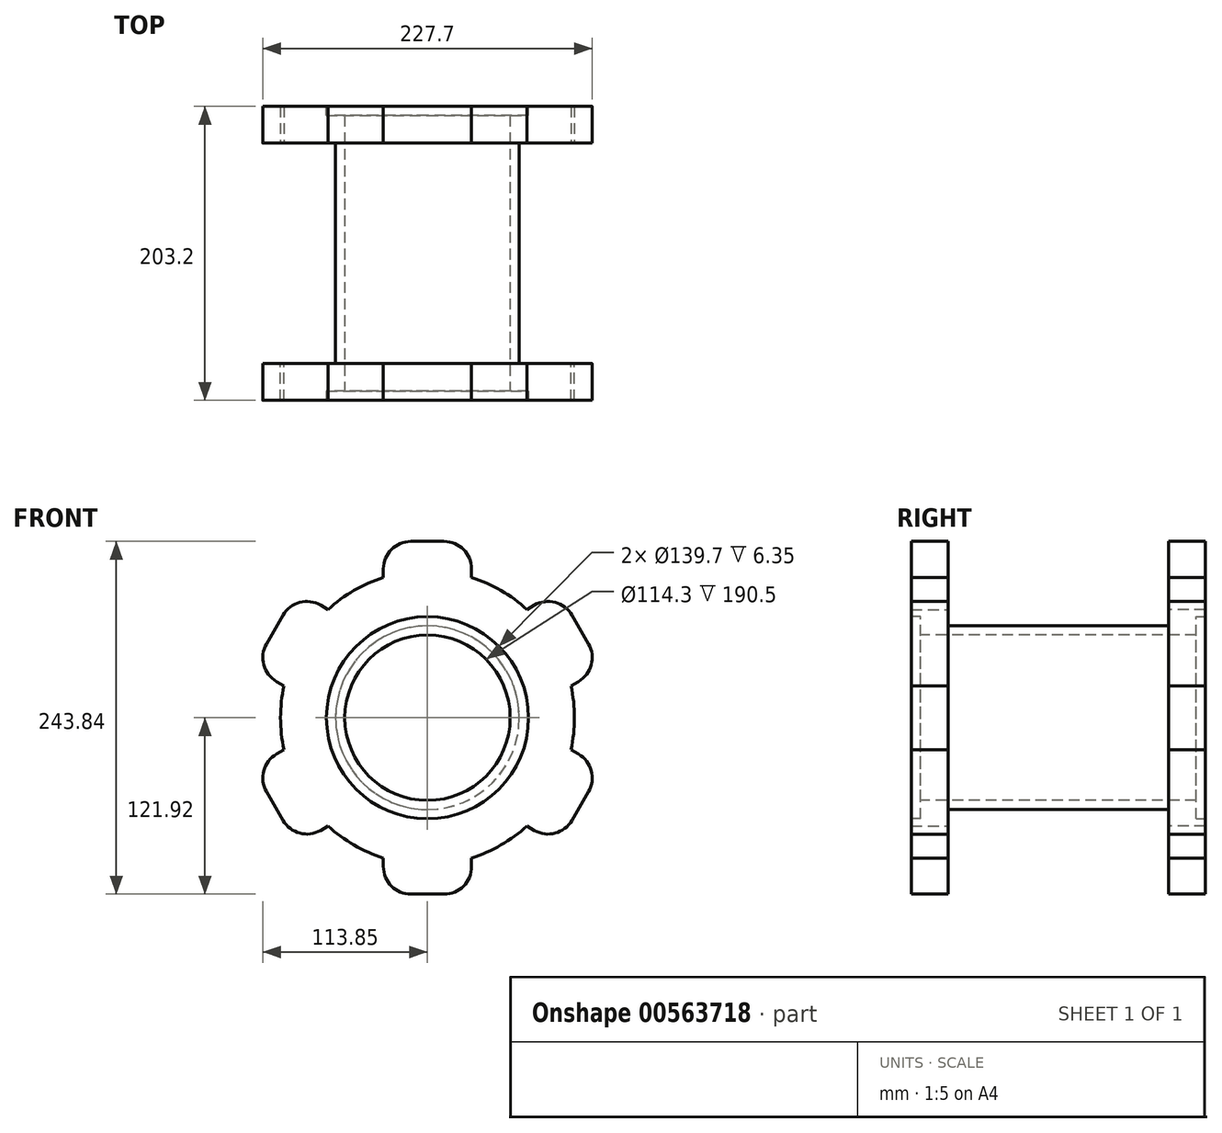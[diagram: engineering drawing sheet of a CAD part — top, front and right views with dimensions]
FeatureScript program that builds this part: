
annotation { "Feature Type Name" : "Feature", "Feature Type Description" : "" }
export const myFeature = defineFeature(function(context is Context, id is Id, definition is map)
    precondition{}
    {
        {
            var Q0;
            Q0=qCreatedBy(makeId("Front.planeOp"),FACE);
            var sketch = newSketch(context, id + "F0", { "sketchPlane" : qUnion([Q0])});
            skCircle(sketch, "E0", {"center": v(0, 0) * mm, "radius": 101.6 * mm});
            skLineSegment(sketch, "E1.top", {"start": v(11.43, 121.92) * mm, "end": v(-11.43, 121.92) * mm});
            skLineSegment(sketch, "E1.left", {"start": v(30.48, 96.92) * mm, "end": v(30.48, 102.87) * mm});
            skLineSegment(sketch, "E1.right", {"start": v(-30.48, 96.92) * mm, "end": v(-30.48, 102.87) * mm});
            skPoint(sketch, "E2.visualSharp", {"position": v(30.48, 121.92) * mm});
            skArc(sketch, "E2.filletArc", {"start": v(30.48, 102.87) * mm, "mid": v(24.9, 116.34) * mm, "end": v(11.43, 121.92) * mm});
            skPoint(sketch, "E3.visualSharp", {"position": v(-30.48, 121.92) * mm});
            skArc(sketch, "E3.filletArc", {"start": v(-11.43, 121.92) * mm, "mid": v(-24.9, 116.34) * mm, "end": v(-30.48, 102.87) * mm});
            skLineSegment(sketch, "E4.1.1", {"start": v(-99.18, 22.06) * mm, "end": v(-104.33, 25.04) * mm});
            skPoint(sketch, "E4.1.2", {"position": v(-90.35, 87.36) * mm});
            skLineSegment(sketch, "E4.1.3", {"start": v(-99.87, 70.86) * mm, "end": v(-111.3, 51.06) * mm});
            skPoint(sketch, "E4.1.4", {"position": v(-120.83, 34.56) * mm});
            skArc(sketch, "E4.1.5", {"start": v(-111.3, 51.06) * mm, "mid": v(-113.2, 36.6) * mm, "end": v(-104.33, 25.04) * mm});
            skLineSegment(sketch, "E4.1.6", {"start": v(-68.7, 74.86) * mm, "end": v(-73.85, 77.83) * mm});
            skArc(sketch, "E4.1.7", {"start": v(-73.85, 77.83) * mm, "mid": v(-88.3, 79.73) * mm, "end": v(-99.87, 70.86) * mm});
            skLineSegment(sketch, "E4.2.1", {"start": v(-68.7, -74.86) * mm, "end": v(-73.85, -77.83) * mm});
            skPoint(sketch, "E4.2.2", {"position": v(-120.83, -34.56) * mm});
            skLineSegment(sketch, "E4.2.3", {"start": v(-111.3, -51.06) * mm, "end": v(-99.87, -70.86) * mm});
            skPoint(sketch, "E4.2.4", {"position": v(-90.35, -87.36) * mm});
            skArc(sketch, "E4.2.5", {"start": v(-99.87, -70.86) * mm, "mid": v(-88.3, -79.73) * mm, "end": v(-73.85, -77.83) * mm});
            skLineSegment(sketch, "E4.2.6", {"start": v(-99.18, -22.06) * mm, "end": v(-104.33, -25.04) * mm});
            skArc(sketch, "E4.2.7", {"start": v(-104.33, -25.04) * mm, "mid": v(-113.2, -36.6) * mm, "end": v(-111.3, -51.06) * mm});
            skLineSegment(sketch, "E4.3.1", {"start": v(30.48, -96.92) * mm, "end": v(30.48, -102.87) * mm});
            skPoint(sketch, "E4.3.2", {"position": v(-30.48, -121.92) * mm});
            skLineSegment(sketch, "E4.3.3", {"start": v(-11.43, -121.92) * mm, "end": v(11.43, -121.92) * mm});
            skPoint(sketch, "E4.3.4", {"position": v(30.48, -121.92) * mm});
            skArc(sketch, "E4.3.5", {"start": v(11.43, -121.92) * mm, "mid": v(24.9, -116.34) * mm, "end": v(30.48, -102.87) * mm});
            skLineSegment(sketch, "E4.3.6", {"start": v(-30.48, -96.92) * mm, "end": v(-30.48, -102.87) * mm});
            skArc(sketch, "E4.3.7", {"start": v(-30.48, -102.87) * mm, "mid": v(-24.9, -116.34) * mm, "end": v(-11.43, -121.92) * mm});
            skLineSegment(sketch, "E4.4.1", {"start": v(99.18, -22.06) * mm, "end": v(104.33, -25.04) * mm});
            skPoint(sketch, "E4.4.2", {"position": v(90.35, -87.36) * mm});
            skLineSegment(sketch, "E4.4.3", {"start": v(99.87, -70.86) * mm, "end": v(111.3, -51.06) * mm});
            skPoint(sketch, "E4.4.4", {"position": v(120.83, -34.56) * mm});
            skArc(sketch, "E4.4.5", {"start": v(111.3, -51.06) * mm, "mid": v(113.2, -36.6) * mm, "end": v(104.33, -25.04) * mm});
            skLineSegment(sketch, "E4.4.6", {"start": v(68.7, -74.86) * mm, "end": v(73.85, -77.83) * mm});
            skArc(sketch, "E4.4.7", {"start": v(73.85, -77.83) * mm, "mid": v(88.3, -79.73) * mm, "end": v(99.87, -70.86) * mm});
            skLineSegment(sketch, "E4.5.1", {"start": v(68.7, 74.86) * mm, "end": v(73.85, 77.83) * mm});
            skPoint(sketch, "E4.5.2", {"position": v(120.83, 34.56) * mm});
            skLineSegment(sketch, "E4.5.3", {"start": v(111.3, 51.06) * mm, "end": v(99.87, 70.86) * mm});
            skPoint(sketch, "E4.5.4", {"position": v(90.35, 87.36) * mm});
            skArc(sketch, "E4.5.5", {"start": v(99.87, 70.86) * mm, "mid": v(88.3, 79.73) * mm, "end": v(73.85, 77.83) * mm});
            skLineSegment(sketch, "E4.5.6", {"start": v(99.18, 22.06) * mm, "end": v(104.33, 25.04) * mm});
            skArc(sketch, "E4.5.7", {"start": v(104.33, 25.04) * mm, "mid": v(113.2, 36.6) * mm, "end": v(111.3, 51.06) * mm});
            skSolve(sketch);
        }
        {
            var Q0;
            {var subQ0=sQuery(id+"F0.wireOp",EDGE,"E0");var subQ1=makeQuery(id+"F0.imprint","INTERSECT",VERTEX,{"derivedFrom":[subQ0,sQuery(id+"F0.wireOp",EDGE,"E1.left")]});Q0=makeQuery(id+"F0.imprint","IMPRINT",FACE,{"disambiguationData":[TD([[makeQuery(id+"F0.imprint","IMPRINT",EDGE,{"disambiguationData":[TD([[subQ1,-1.0]])],"derivedFrom":subQ0}),1.0]])]});}
            var Q1;
            Q1=makeQuery(id+"F0.imprint","IMPRINT",FACE,{"disambiguationData":[TD([[makeQuery(id+"F0.imprint","IMPRINT",EDGE,{"derivedFrom":sQuery(id+"F0.wireOp",EDGE,"E1.top")}),1.0]])]});
            var Q2;
            {var subQ0=sQuery(id+"F0.wireOp",EDGE,"E0");var subQ8=makeQuery(id+"F0.imprint","INTERSECT",VERTEX,{"derivedFrom":[sQuery(id+"F0.wireOp",EDGE,"E4.4.1"),subQ0]});Q2=makeQuery(id+"F0.imprint","IMPRINT",FACE,{"disambiguationData":[TD([[makeQuery(id+"F0.imprint","IMPRINT",EDGE,{"disambiguationData":[TD([[subQ8,1.0]])],"derivedFrom":subQ0}),1.0]])]});}
            var Q3;
            {var subQ0=sQuery(id+"F0.wireOp",EDGE,"E4.5.1");Q3=makeQuery(id+"F0.imprint","IMPRINT",FACE,{"disambiguationData":[TD([[makeQuery(id+"F0.imprint","IMPRINT",EDGE,{"derivedFrom":subQ0}),-1.0]])]});}
            var Q4;
            {var subQ1=sQuery(id+"F0.wireOp",EDGE,"E4.4.1");Q4=makeQuery(id+"F0.imprint","IMPRINT",FACE,{"disambiguationData":[TD([[makeQuery(id+"F0.imprint","IMPRINT",EDGE,{"derivedFrom":subQ1}),-1.0]])]});}
            var Q5;
            {var subQ1=sQuery(id+"F0.wireOp",EDGE,"E4.3.1");Q5=makeQuery(id+"F0.imprint","IMPRINT",FACE,{"disambiguationData":[TD([[makeQuery(id+"F0.imprint","IMPRINT",EDGE,{"derivedFrom":subQ1}),-1.0]])]});}
            var Q6;
            {var subQ1=sQuery(id+"F0.wireOp",EDGE,"E4.2.1");Q6=makeQuery(id+"F0.imprint","IMPRINT",FACE,{"disambiguationData":[TD([[makeQuery(id+"F0.imprint","IMPRINT",EDGE,{"derivedFrom":subQ1}),-1.0]])]});}
            var Q7;
            {var subQ2=sQuery(id+"F0.wireOp",EDGE,"E4.1.1");Q7=makeQuery(id+"F0.imprint","IMPRINT",FACE,{"disambiguationData":[TD([[makeQuery(id+"F0.imprint","IMPRINT",EDGE,{"derivedFrom":subQ2}),-1.0]])]});}
            extrude(context, id + "F1", {"entities" : qUnion([Q0, Q1, Q2, Q3, Q4, Q5, Q6, Q7]), "depth" : 25.4 * mm});
        }
        {
            var Q0;
            Q0=makeQuery(id+"F1.opExtrude","CAP_FACE",FACE,{"disambiguationData":[OSD([sQuery(id+"F0.wireOp",EDGE,"E1.top"),sQuery(id+"F0.wireOp",EDGE,"E1.left"),sQuery(id+"F0.wireOp",EDGE,"E1.right"),sQuery(id+"F0.wireOp",EDGE,"E2.filletArc"),sQuery(id+"F0.wireOp",EDGE,"E3.filletArc"),sQuery(id+"F0.wireOp",EDGE,"E4.1.1"),sQuery(id+"F0.wireOp",EDGE,"E4.1.3"),sQuery(id+"F0.wireOp",EDGE,"E4.1.5"),sQuery(id+"F0.wireOp",EDGE,"E4.1.6"),sQuery(id+"F0.wireOp",EDGE,"E4.1.7"),sQuery(id+"F0.wireOp",EDGE,"E4.2.1"),sQuery(id+"F0.wireOp",EDGE,"E4.2.3"),sQuery(id+"F0.wireOp",EDGE,"E4.2.5"),sQuery(id+"F0.wireOp",EDGE,"E4.2.6"),sQuery(id+"F0.wireOp",EDGE,"E4.2.7"),sQuery(id+"F0.wireOp",EDGE,"E4.3.1"),sQuery(id+"F0.wireOp",EDGE,"E4.3.3"),sQuery(id+"F0.wireOp",EDGE,"E4.3.5"),sQuery(id+"F0.wireOp",EDGE,"E4.3.6"),sQuery(id+"F0.wireOp",EDGE,"E4.3.7"),sQuery(id+"F0.wireOp",EDGE,"E4.4.1"),sQuery(id+"F0.wireOp",EDGE,"E4.4.3"),sQuery(id+"F0.wireOp",EDGE,"E4.4.5"),sQuery(id+"F0.wireOp",EDGE,"E4.4.6"),sQuery(id+"F0.wireOp",EDGE,"E4.4.7"),sQuery(id+"F0.wireOp",EDGE,"E0"),sQuery(id+"F0.wireOp",EDGE,"E4.5.1"),sQuery(id+"F0.wireOp",EDGE,"E4.5.3"),sQuery(id+"F0.wireOp",EDGE,"E4.5.5"),sQuery(id+"F0.wireOp",EDGE,"E4.5.6"),sQuery(id+"F0.wireOp",EDGE,"E4.5.7")])],"isStart":true});
            var sketch = newSketch(context, id + "F2", { "sketchPlane" : qUnion([Q0])});
            skCircle(sketch, "E5", {"center": v(0, 0) * mm, "radius": 63.5 * mm});
            skSolve(sketch);
        }
        {
            var Q0;
            Q0=qSketchRegion(id+"F2",true);
            extrude(context, id + "F3", {"entities" : qUnion([Q0]), "operationType" : NewBodyOperationType.ADD, "depth" : 152.4 * mm});
        }
        {
            var Q0;
            Q0=makeQuery(id+"F1.opExtrude","CAP_FACE",FACE,{"disambiguationData":[OSD([sQuery(id+"F0.wireOp",EDGE,"E1.top"),sQuery(id+"F0.wireOp",EDGE,"E1.left"),sQuery(id+"F0.wireOp",EDGE,"E1.right"),sQuery(id+"F0.wireOp",EDGE,"E2.filletArc"),sQuery(id+"F0.wireOp",EDGE,"E3.filletArc"),sQuery(id+"F0.wireOp",EDGE,"E4.1.1"),sQuery(id+"F0.wireOp",EDGE,"E4.1.3"),sQuery(id+"F0.wireOp",EDGE,"E4.1.5"),sQuery(id+"F0.wireOp",EDGE,"E4.1.6"),sQuery(id+"F0.wireOp",EDGE,"E4.1.7"),sQuery(id+"F0.wireOp",EDGE,"E4.2.1"),sQuery(id+"F0.wireOp",EDGE,"E4.2.3"),sQuery(id+"F0.wireOp",EDGE,"E4.2.5"),sQuery(id+"F0.wireOp",EDGE,"E4.2.6"),sQuery(id+"F0.wireOp",EDGE,"E4.2.7"),sQuery(id+"F0.wireOp",EDGE,"E4.3.1"),sQuery(id+"F0.wireOp",EDGE,"E4.3.3"),sQuery(id+"F0.wireOp",EDGE,"E4.3.5"),sQuery(id+"F0.wireOp",EDGE,"E4.3.6"),sQuery(id+"F0.wireOp",EDGE,"E4.3.7"),sQuery(id+"F0.wireOp",EDGE,"E4.4.1"),sQuery(id+"F0.wireOp",EDGE,"E4.4.3"),sQuery(id+"F0.wireOp",EDGE,"E4.4.5"),sQuery(id+"F0.wireOp",EDGE,"E4.4.6"),sQuery(id+"F0.wireOp",EDGE,"E4.4.7"),sQuery(id+"F0.wireOp",EDGE,"E0"),sQuery(id+"F0.wireOp",EDGE,"E4.5.1"),sQuery(id+"F0.wireOp",EDGE,"E4.5.3"),sQuery(id+"F0.wireOp",EDGE,"E4.5.5"),sQuery(id+"F0.wireOp",EDGE,"E4.5.6"),sQuery(id+"F0.wireOp",EDGE,"E4.5.7")])],"isStart":true});
            cPlane(context, id + "F4", {"entities" : qUnion([Q0]), "cplaneType" : CPlaneType.OFFSET, "offset" : 76.2 * mm, "width" : 152.4 * mm, "height" : 152.4 * mm});
        }
        {
            var Q0;
            Q0=makeQuery(id+"F1.opExtrude","SWEPT_BODY",BODY,{"disambiguationData":[OSD([sQuery(id+"F0.wireOp",EDGE,"E1.top"),sQuery(id+"F0.wireOp",EDGE,"E1.left"),sQuery(id+"F0.wireOp",EDGE,"E1.right"),sQuery(id+"F0.wireOp",EDGE,"E2.filletArc"),sQuery(id+"F0.wireOp",EDGE,"E3.filletArc"),sQuery(id+"F0.wireOp",EDGE,"E4.1.1"),sQuery(id+"F0.wireOp",EDGE,"E4.1.3"),sQuery(id+"F0.wireOp",EDGE,"E4.1.5"),sQuery(id+"F0.wireOp",EDGE,"E4.1.6"),sQuery(id+"F0.wireOp",EDGE,"E4.1.7"),sQuery(id+"F0.wireOp",EDGE,"E4.2.1"),sQuery(id+"F0.wireOp",EDGE,"E4.2.3"),sQuery(id+"F0.wireOp",EDGE,"E4.2.5"),sQuery(id+"F0.wireOp",EDGE,"E4.2.6"),sQuery(id+"F0.wireOp",EDGE,"E4.2.7"),sQuery(id+"F0.wireOp",EDGE,"E4.3.1"),sQuery(id+"F0.wireOp",EDGE,"E4.3.3"),sQuery(id+"F0.wireOp",EDGE,"E4.3.5"),sQuery(id+"F0.wireOp",EDGE,"E4.3.6"),sQuery(id+"F0.wireOp",EDGE,"E4.3.7"),sQuery(id+"F0.wireOp",EDGE,"E4.4.1"),sQuery(id+"F0.wireOp",EDGE,"E4.4.3"),sQuery(id+"F0.wireOp",EDGE,"E4.4.5"),sQuery(id+"F0.wireOp",EDGE,"E4.4.6"),sQuery(id+"F0.wireOp",EDGE,"E4.4.7"),sQuery(id+"F0.wireOp",EDGE,"E0"),sQuery(id+"F0.wireOp",EDGE,"E4.5.1"),sQuery(id+"F0.wireOp",EDGE,"E4.5.3"),sQuery(id+"F0.wireOp",EDGE,"E4.5.5"),sQuery(id+"F0.wireOp",EDGE,"E4.5.6"),sQuery(id+"F0.wireOp",EDGE,"E4.5.7")])]});
            var Q1;
            Q1=qCreatedBy(id+"F4.planeOp",FACE);
            mirror(context, id + "F5", {"operationType" : NewBodyOperationType.ADD, "entities" : qUnion([Q0]), "mirrorPlane" : qUnion([Q1])});
        }
        {
            var Q0;
            Q0=makeQuery(id+"F1.opExtrude","CAP_FACE",FACE,{"disambiguationData":[OSD([sQuery(id+"F0.wireOp",EDGE,"E1.top"),sQuery(id+"F0.wireOp",EDGE,"E1.left"),sQuery(id+"F0.wireOp",EDGE,"E1.right"),sQuery(id+"F0.wireOp",EDGE,"E2.filletArc"),sQuery(id+"F0.wireOp",EDGE,"E3.filletArc"),sQuery(id+"F0.wireOp",EDGE,"E4.1.1"),sQuery(id+"F0.wireOp",EDGE,"E4.1.3"),sQuery(id+"F0.wireOp",EDGE,"E4.1.5"),sQuery(id+"F0.wireOp",EDGE,"E4.1.6"),sQuery(id+"F0.wireOp",EDGE,"E4.1.7"),sQuery(id+"F0.wireOp",EDGE,"E4.2.1"),sQuery(id+"F0.wireOp",EDGE,"E4.2.3"),sQuery(id+"F0.wireOp",EDGE,"E4.2.5"),sQuery(id+"F0.wireOp",EDGE,"E4.2.6"),sQuery(id+"F0.wireOp",EDGE,"E4.2.7"),sQuery(id+"F0.wireOp",EDGE,"E4.3.1"),sQuery(id+"F0.wireOp",EDGE,"E4.3.3"),sQuery(id+"F0.wireOp",EDGE,"E4.3.5"),sQuery(id+"F0.wireOp",EDGE,"E4.3.6"),sQuery(id+"F0.wireOp",EDGE,"E4.3.7"),sQuery(id+"F0.wireOp",EDGE,"E4.4.1"),sQuery(id+"F0.wireOp",EDGE,"E4.4.3"),sQuery(id+"F0.wireOp",EDGE,"E4.4.5"),sQuery(id+"F0.wireOp",EDGE,"E4.4.6"),sQuery(id+"F0.wireOp",EDGE,"E4.4.7"),sQuery(id+"F0.wireOp",EDGE,"E0"),sQuery(id+"F0.wireOp",EDGE,"E4.5.1"),sQuery(id+"F0.wireOp",EDGE,"E4.5.3"),sQuery(id+"F0.wireOp",EDGE,"E4.5.5"),sQuery(id+"F0.wireOp",EDGE,"E4.5.6"),sQuery(id+"F0.wireOp",EDGE,"E4.5.7")])],"isStart":false});
            var sketch = newSketch(context, id + "F6", { "sketchPlane" : qUnion([Q0])});
            skCircle(sketch, "E6", {"center": v(0, 0) * mm, "radius": 57.15 * mm});
            skSolve(sketch);
        }
        {
            var Q0;
            Q0=makeQuery(id+"F6.imprint","IMPRINT",FACE,{"disambiguationData":[TD([[makeQuery(id+"F6.imprint","IMPRINT",EDGE,{"derivedFrom":sQuery(id+"F6.wireOp",EDGE,"E6")}),1.0]])]});
            extrude(context, id + "F7", {"entities" : qUnion([Q0]), "operationType" : NewBodyOperationType.REMOVE, "oppositeDirection" : true, "depth" : 228.6 * mm});
        }
        {
            var Q0;
            Q0=makeQuery(id+"F1.opExtrude","CAP_FACE",FACE,{"disambiguationData":[OSD([sQuery(id+"F0.wireOp",EDGE,"E1.top"),sQuery(id+"F0.wireOp",EDGE,"E1.left"),sQuery(id+"F0.wireOp",EDGE,"E1.right"),sQuery(id+"F0.wireOp",EDGE,"E2.filletArc"),sQuery(id+"F0.wireOp",EDGE,"E3.filletArc"),sQuery(id+"F0.wireOp",EDGE,"E4.1.1"),sQuery(id+"F0.wireOp",EDGE,"E4.1.3"),sQuery(id+"F0.wireOp",EDGE,"E4.1.5"),sQuery(id+"F0.wireOp",EDGE,"E4.1.6"),sQuery(id+"F0.wireOp",EDGE,"E4.1.7"),sQuery(id+"F0.wireOp",EDGE,"E4.2.1"),sQuery(id+"F0.wireOp",EDGE,"E4.2.3"),sQuery(id+"F0.wireOp",EDGE,"E4.2.5"),sQuery(id+"F0.wireOp",EDGE,"E4.2.6"),sQuery(id+"F0.wireOp",EDGE,"E4.2.7"),sQuery(id+"F0.wireOp",EDGE,"E4.3.1"),sQuery(id+"F0.wireOp",EDGE,"E4.3.3"),sQuery(id+"F0.wireOp",EDGE,"E4.3.5"),sQuery(id+"F0.wireOp",EDGE,"E4.3.6"),sQuery(id+"F0.wireOp",EDGE,"E4.3.7"),sQuery(id+"F0.wireOp",EDGE,"E4.4.1"),sQuery(id+"F0.wireOp",EDGE,"E4.4.3"),sQuery(id+"F0.wireOp",EDGE,"E4.4.5"),sQuery(id+"F0.wireOp",EDGE,"E4.4.6"),sQuery(id+"F0.wireOp",EDGE,"E4.4.7"),sQuery(id+"F0.wireOp",EDGE,"E0"),sQuery(id+"F0.wireOp",EDGE,"E4.5.1"),sQuery(id+"F0.wireOp",EDGE,"E4.5.3"),sQuery(id+"F0.wireOp",EDGE,"E4.5.5"),sQuery(id+"F0.wireOp",EDGE,"E4.5.6"),sQuery(id+"F0.wireOp",EDGE,"E4.5.7")])],"isStart":false});
            var sketch = newSketch(context, id + "F8", { "sketchPlane" : qUnion([Q0])});
            skCircle(sketch, "E7", {"center": v(0, 0) * mm, "radius": 69.85 * mm});
            skSolve(sketch);
        }
        {
            var Q0;
            Q0=makeQuery(id+"F8.imprint","IMPRINT",FACE,{"disambiguationData":[TD([[makeQuery(id+"F8.imprint","IMPRINT",EDGE,{"derivedFrom":sQuery(id+"F8.wireOp",EDGE,"E7")}),1.0]])]});
            extrude(context, id + "F9", {"entities" : qUnion([Q0]), "operationType" : NewBodyOperationType.REMOVE, "oppositeDirection" : true, "depth" : 6.35 * mm});
        }
        {
            var Q0;
            Q0=makeQuery(id+"F1.opExtrude","SWEPT_BODY",BODY,{"disambiguationData":[OSD([sQuery(id+"F0.wireOp",EDGE,"E1.top"),sQuery(id+"F0.wireOp",EDGE,"E1.left"),sQuery(id+"F0.wireOp",EDGE,"E1.right"),sQuery(id+"F0.wireOp",EDGE,"E2.filletArc"),sQuery(id+"F0.wireOp",EDGE,"E3.filletArc"),sQuery(id+"F0.wireOp",EDGE,"E4.1.1"),sQuery(id+"F0.wireOp",EDGE,"E4.1.3"),sQuery(id+"F0.wireOp",EDGE,"E4.1.5"),sQuery(id+"F0.wireOp",EDGE,"E4.1.6"),sQuery(id+"F0.wireOp",EDGE,"E4.1.7"),sQuery(id+"F0.wireOp",EDGE,"E4.2.1"),sQuery(id+"F0.wireOp",EDGE,"E4.2.3"),sQuery(id+"F0.wireOp",EDGE,"E4.2.5"),sQuery(id+"F0.wireOp",EDGE,"E4.2.6"),sQuery(id+"F0.wireOp",EDGE,"E4.2.7"),sQuery(id+"F0.wireOp",EDGE,"E4.3.1"),sQuery(id+"F0.wireOp",EDGE,"E4.3.3"),sQuery(id+"F0.wireOp",EDGE,"E4.3.5"),sQuery(id+"F0.wireOp",EDGE,"E4.3.6"),sQuery(id+"F0.wireOp",EDGE,"E4.3.7"),sQuery(id+"F0.wireOp",EDGE,"E4.4.1"),sQuery(id+"F0.wireOp",EDGE,"E4.4.3"),sQuery(id+"F0.wireOp",EDGE,"E4.4.5"),sQuery(id+"F0.wireOp",EDGE,"E4.4.6"),sQuery(id+"F0.wireOp",EDGE,"E4.4.7"),sQuery(id+"F0.wireOp",EDGE,"E0"),sQuery(id+"F0.wireOp",EDGE,"E4.5.1"),sQuery(id+"F0.wireOp",EDGE,"E4.5.3"),sQuery(id+"F0.wireOp",EDGE,"E4.5.5"),sQuery(id+"F0.wireOp",EDGE,"E4.5.6"),sQuery(id+"F0.wireOp",EDGE,"E4.5.7")])]});
            var Q1;
            Q1=qCreatedBy(id+"F4.planeOp",FACE);
            mirror(context, id + "F10", {"operationType" : NewBodyOperationType.INTERSECT, "entities" : qUnion([Q0]), "mirrorPlane" : qUnion([Q1])});
        }
    });
